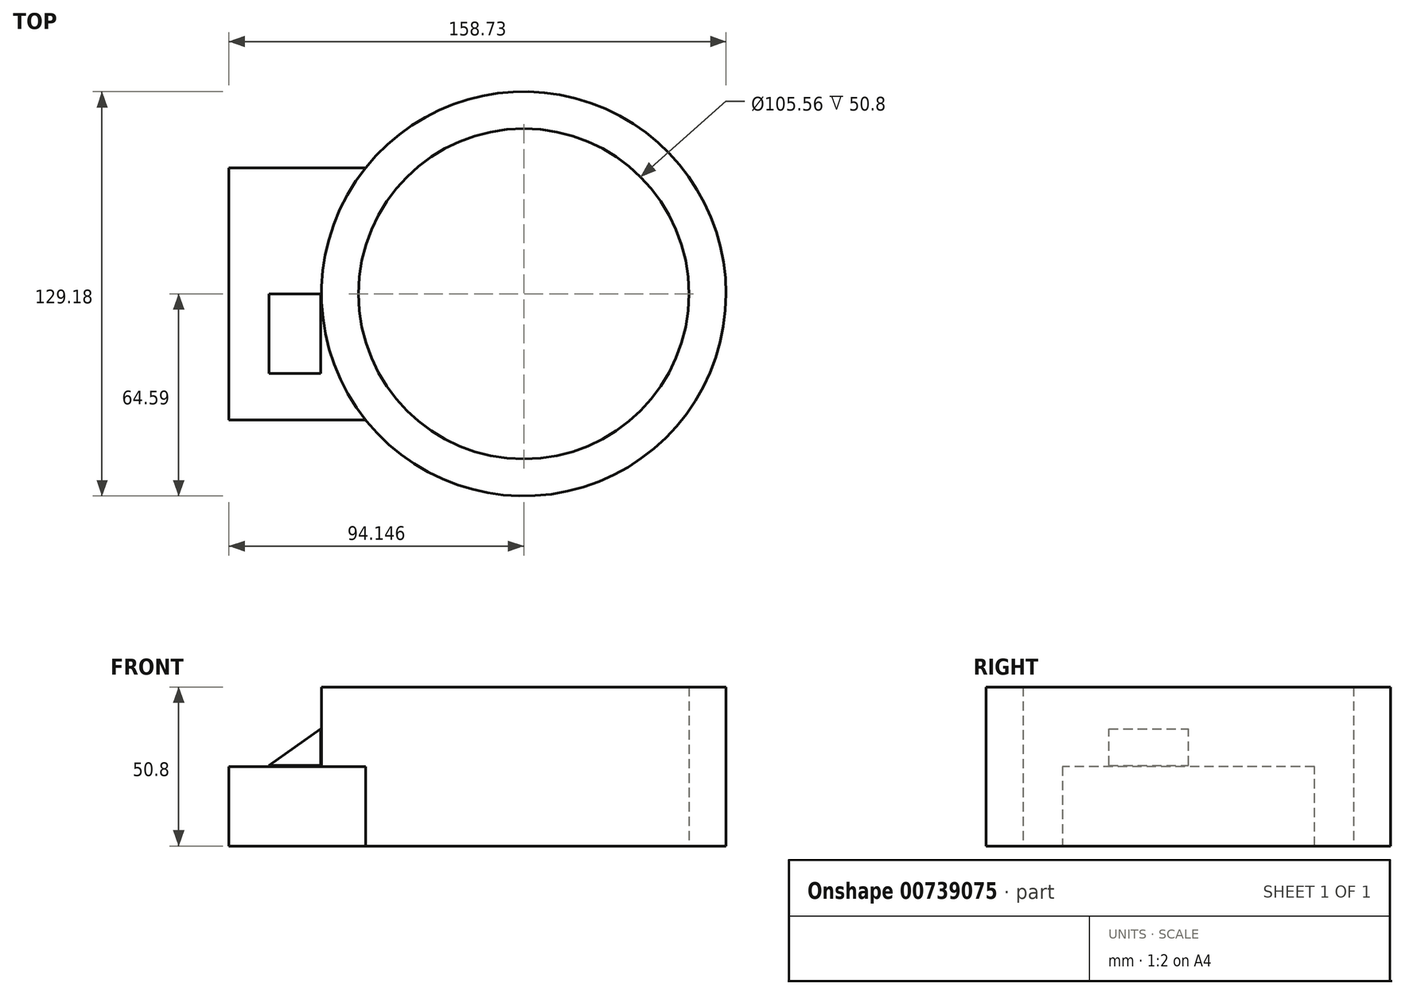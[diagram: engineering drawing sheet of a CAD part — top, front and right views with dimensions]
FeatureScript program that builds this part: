
annotation { "Feature Type Name" : "Feature", "Feature Type Description" : "" }
export const myFeature = defineFeature(function(context is Context, id is Id, definition is map)
    precondition{}
    {
        {
            var Q0;
            Q0=qCreatedBy(makeId("Top.planeOp"),FACE);
            var sketch = newSketch(context, id + "F0", { "sketchPlane" : qUnion([Q0])});
            skLineSegment(sketch, "E0.bottom", {"start": v(-59.1, 40.27) * mm, "end": v(59.1, 40.27) * mm});
            skLineSegment(sketch, "E0.top", {"start": v(-59.1, -40.27) * mm, "end": v(59.1, -40.27) * mm});
            skLineSegment(sketch, "E0.left", {"start": v(-59.1, 40.27) * mm, "end": v(-59.1, -40.27) * mm});
            skLineSegment(sketch, "E0.right", {"start": v(59.1, 40.27) * mm, "end": v(59.1, -40.27) * mm});
            skPoint(sketch, "E0.middle", {"position": v(0, 0) * mm});
            skSolve(sketch);
        }
        {
            var Q0;
            Q0 = qSketchRegion(id + "F0", true);
            extrude(context, id + "F1", {"entities" : qUnion([Q0]), "depth" : 25.4 * mm, "offsetDistance" : 25.4 * mm});
        }
        {
            var Q0;
            Q0=makeQuery(id+"F1.opExtrude","CAP_FACE",FACE,{"disambiguationData":[OSD([sQuery(id+"F0.wireOp",EDGE,"E0.bottom"),sQuery(id+"F0.wireOp",EDGE,"E0.top"),sQuery(id+"F0.wireOp",EDGE,"E0.left"),sQuery(id+"F0.wireOp",EDGE,"E0.right")])],"isStart":false});
            var sketch = newSketch(context, id + "F2", { "sketchPlane" : qUnion([Q0])});
            skCircle(sketch, "E1", {"center": v(35.04, 0) * mm, "radius": 64.59 * mm});
            skCircle(sketch, "E2", {"center": v(35.04, 0) * mm, "radius": 52.78 * mm});
            skSolve(sketch);
        }
        {
            var Q0;
            {var subQ0=sQuery(id+"F2.wireOp",EDGE,"E1");var subQ1=makeQuery(id+"F1.opExtrude","CAP_EDGE",EDGE,{"disambiguationData":[OSD([sQuery(id+"F0.wireOp",EDGE,"E0.bottom")])],"isStart":false});var subQ2=makeQuery(id+"F2.imprint","INTERSECT",VERTEX,{"derivedFrom":[subQ1,subQ0]});Q0=makeQuery(id+"F2.imprint","IMPRINT",FACE,{"disambiguationData":[TD([[makeQuery(id+"F2.imprint","IMPRINT",EDGE,{"disambiguationData":[TD([[subQ2,-1.0]])],"derivedFrom":subQ0}),1.0]])]});}
            var Q1;
            {var subQ0=sQuery(id+"F2.wireOp",EDGE,"E1");var subQ1=makeQuery(id+"F1.opExtrude","CAP_EDGE",EDGE,{"disambiguationData":[OSD([sQuery(id+"F0.wireOp",EDGE,"E0.bottom")])],"isStart":false});var subQ2=makeQuery(id+"F2.imprint","INTERSECT",VERTEX,{"derivedFrom":[subQ1,subQ0]});Q1=makeQuery(id+"F2.imprint","IMPRINT",FACE,{"disambiguationData":[TD([[makeQuery(id+"F2.imprint","IMPRINT",EDGE,{"disambiguationData":[TD([[subQ2,1.0]])],"derivedFrom":subQ0}),1.0]])]});}
            extrude(context, id + "F3", {"entities" : qUnion([Q0, Q1]), "operationType" : NewBodyOperationType.ADD, "depth" : 25.4 * mm, "offsetDistance" : 25.4 * mm});
        }
        {
            var Q0;
            {var subQ1=sQuery(id+"F0.wireOp",EDGE,"E0.top");var subQ2=sQuery(id+"F0.wireOp",EDGE,"E0.right");var subQ3=sQuery(id+"F0.wireOp",EDGE,"E0.bottom");Q0=makeQuery(id+"F3.boolean.opBoolean","SPLIT",FACE,{"disambiguationData":[TD([makeQuery(id+"F1.opExtrude","SWEPT_FACE",FACE,{"disambiguationData":[OSD([subQ2])]})])],"derivedFrom":makeQuery(id+"F1.opExtrude","CAP_FACE",FACE,{"disambiguationData":[OSD([subQ3,subQ1,sQuery(id+"F0.wireOp",EDGE,"E0.left"),subQ2])],"isStart":false})});}
            extrude(context, id + "F4", {"entities" : qUnion([Q0]), "operationType" : NewBodyOperationType.REMOVE, "oppositeDirection" : true, "depth" : 25.4 * mm, "offsetDistance" : 25.4 * mm});
        }
        {
            var Q0;
            Q0=makeQuery(id+"F3.opExtrude","CAP_FACE",FACE,{"disambiguationData":[OSD([sQuery(id+"F2.wireOp",EDGE,"E1"),sQuery(id+"F2.wireOp",EDGE,"E2")])],"isStart":true});
            extrude(context, id + "F5", {"entities" : qUnion([Q0]), "operationType" : NewBodyOperationType.ADD, "depth" : 25.4 * mm, "offsetDistance" : 25.4 * mm});
        }
        {
            var Q0;
            Q0=qCreatedBy(makeId("Front.planeOp"),FACE);
            var sketch = newSketch(context, id + "F6", { "sketchPlane" : qUnion([Q0])});
            skLineSegment(sketch, "E3", {"start": v(-29.83, 37.38) * mm, "end": v(-46.3, 25.78) * mm});
            skLineSegment(sketch, "E4", {"start": v(-46.3, 25.78) * mm, "end": v(-29.83, 25.78) * mm});
            skLineSegment(sketch, "E5", {"start": v(-29.83, 25.78) * mm, "end": v(-29.83, 37.38) * mm});
            skSolve(sketch);
        }
        {
            var Q0;
            Q0 = qSketchRegion(id + "F6", true);
            extrude(context, id + "F7", {"entities" : qUnion([Q0]), "depth" : 25.4 * mm, "offsetDistance" : 25.4 * mm});
        }
    });
